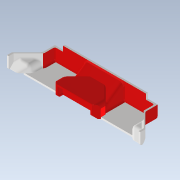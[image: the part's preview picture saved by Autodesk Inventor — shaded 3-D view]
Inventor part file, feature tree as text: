
AUTODESK INVENTOR PART (.ipt)
format: ipt  version: 2022.1 (Build 261234020, 234B)  size: 1,107,456 bytes
history: native  units: mm
features: extrude x1, sketch x1
ambient origin geometry x8: Origin, YZ Plane, XZ Plane, XY Plane, X Axis, Y Axis, Z Axis, Center Point
bodies: Volumenkörper2 (feature_tree), Volumenkörper1 (feature_tree)
feature tree (2):
  extrude  "Extrusion1"  Depth=1.0mm
  sketch  "Skizze1"  dims[d0=1.0mm d1=1.0mm d2=170.0mm d3=38.521424mm d4=38.521424mm d5=70.0mm d6=0.0mm d7=0.0mm]
